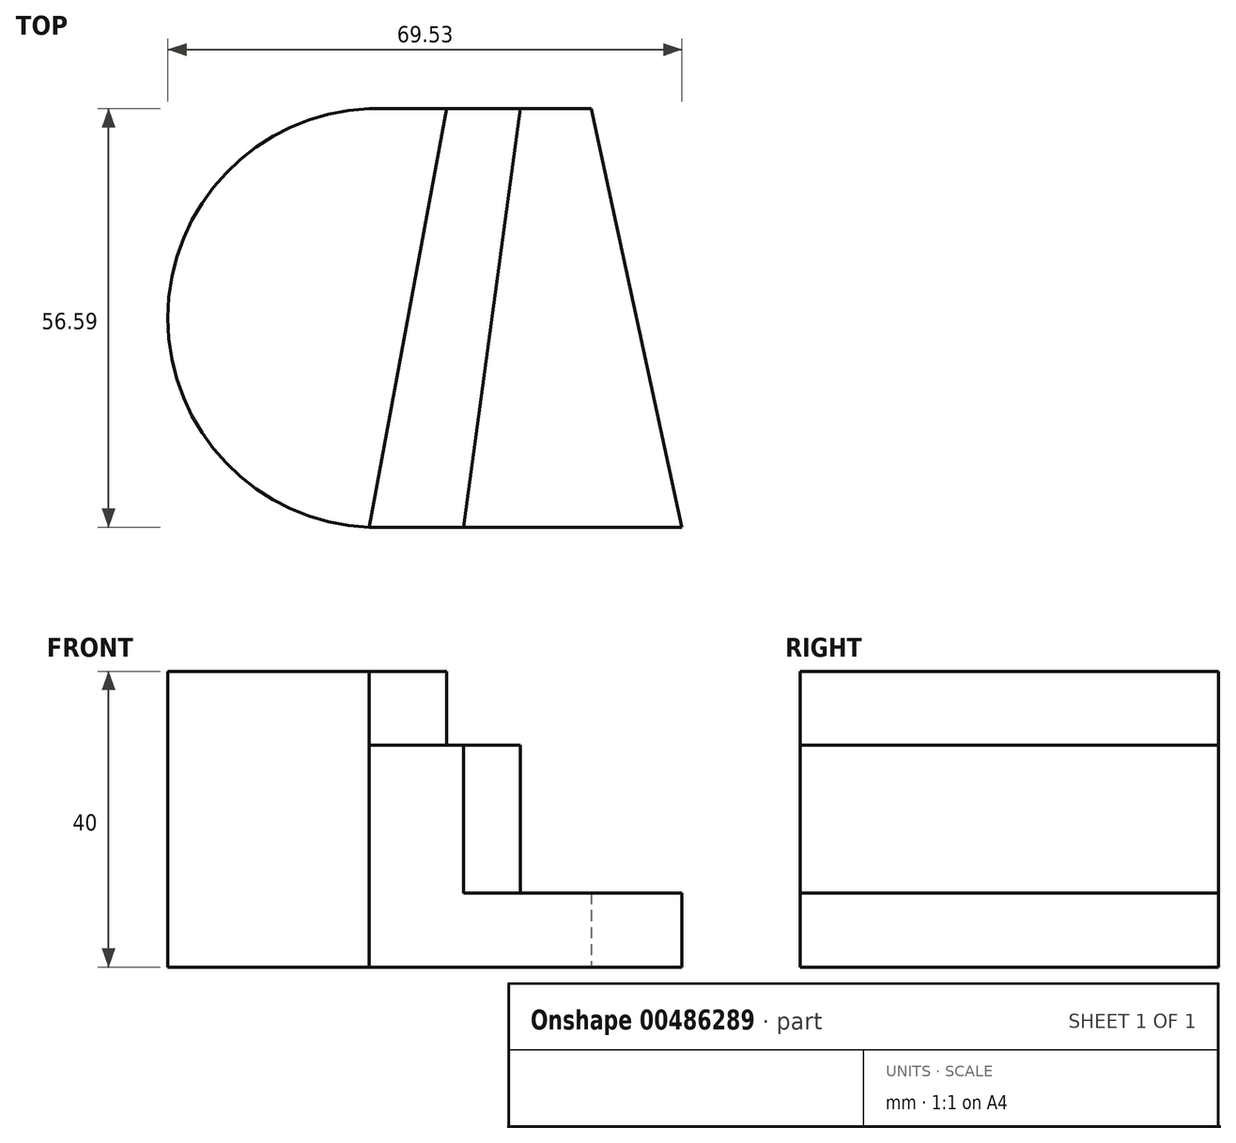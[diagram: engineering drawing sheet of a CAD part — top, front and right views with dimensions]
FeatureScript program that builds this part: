
annotation { "Feature Type Name" : "Feature", "Feature Type Description" : "" }
export const myFeature = defineFeature(function(context is Context, id is Id, definition is map)
    precondition{}
    {
        {
            var Q0;
            Q0=qCreatedBy(makeId("Top.planeOp"),FACE);
            var sketch = newSketch(context, id + "F0", { "sketchPlane" : qUnion([Q0])});
            skLineSegment(sketch, "E0", {"start": v(9.57, 38.72) * mm, "end": v(21.85, -17.87) * mm});
            skLineSegment(sketch, "E1", {"start": v(21.85, -17.87) * mm, "end": v(-7.67, -17.87) * mm});
            skLineSegment(sketch, "E2", {"start": v(-7.67, -17.87) * mm, "end": v(0, 38.72) * mm});
            skLineSegment(sketch, "E3", {"start": v(0, 38.72) * mm, "end": v(9.57, 38.72) * mm});
            skLineSegment(sketch, "E4", {"start": v(0, 38.72) * mm, "end": v(-10, 38.72) * mm});
            skLineSegment(sketch, "E5", {"start": v(-10, 38.72) * mm, "end": v(-20.43, -17.87) * mm});
            skLineSegment(sketch, "E6", {"start": v(-20.43, -17.87) * mm, "end": v(-7.67, -17.87) * mm});
            skLineSegment(sketch, "E7", {"start": v(-10, 38.72) * mm, "end": v(-20.43, 38.72) * mm});
            skArc(sketch, "E8", {"start": v(-20.43, 38.72) * mm, "mid": v(-47.68, 10.43) * mm, "end": v(-20.43, -17.87) * mm});
            skSolve(sketch);
        }
        {
            var Q0;
            Q0=makeQuery(id+"F0.imprint","IMPRINT",FACE,{"disambiguationData":[TD([[makeQuery(id+"F0.imprint","IMPRINT",EDGE,{"derivedFrom":sQuery(id+"F0.wireOp",EDGE,"E0")}),-1.0]])]});
            extrude(context, id + "F1", {"entities" : qUnion([Q0]), "depth" : 10 * mm, "offsetDistance" : 25 * mm});
        }
        {
            var Q0;
            Q0=makeQuery(id+"F0.imprint","IMPRINT",FACE,{"disambiguationData":[TD([[makeQuery(id+"F0.imprint","IMPRINT",EDGE,{"derivedFrom":sQuery(id+"F0.wireOp",EDGE,"E2")}),1.0]])]});
            extrude(context, id + "F2", {"entities" : qUnion([Q0]), "operationType" : NewBodyOperationType.ADD, "depth" : 30 * mm, "offsetDistance" : 25 * mm});
        }
        {
            var Q0;
            Q0=makeQuery(id+"F0.imprint","IMPRINT",FACE,{"disambiguationData":[TD([[makeQuery(id+"F0.imprint","IMPRINT",EDGE,{"derivedFrom":sQuery(id+"F0.wireOp",EDGE,"E5")}),-1.0]])]});
            extrude(context, id + "F3", {"entities" : qUnion([Q0]), "operationType" : NewBodyOperationType.ADD, "depth" : 40 * mm, "offsetDistance" : 25 * mm});
        }
    });
